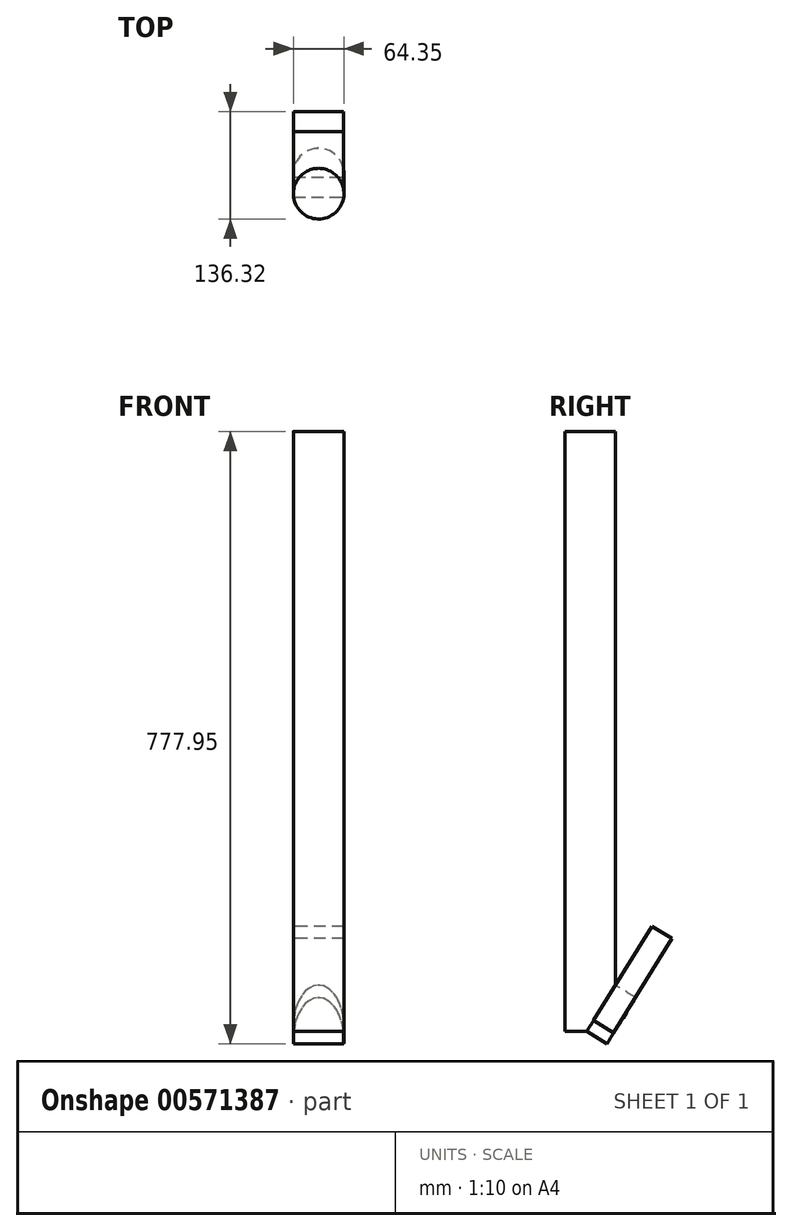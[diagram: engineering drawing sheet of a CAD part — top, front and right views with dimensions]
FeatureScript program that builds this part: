
annotation { "Feature Type Name" : "Feature", "Feature Type Description" : "" }
export const myFeature = defineFeature(function(context is Context, id is Id, definition is map)
    precondition{}
    {
        {
            var Q0;
            Q0=qCreatedBy(makeId("Top.planeOp"),FACE);
            var sketch = newSketch(context, id + "F0", { "sketchPlane" : qUnion([Q0])});
            skCircle(sketch, "E0", {"center": v(-58.01, -56.88) * mm, "radius": 32.18 * mm});
            skSolve(sketch);
        }
        {
            var Q0;
            Q0=makeQuery(id+"F0.imprint","IMPRINT",FACE,{"disambiguationData":[TD([[makeQuery(id+"F0.imprint","IMPRINT",EDGE,{"derivedFrom":sQuery(id+"F0.wireOp",EDGE,"E0")}),1.0]])]});
            extrude(context, id + "F1", {"entities" : qUnion([Q0]), "depth" : 762 * mm, "offsetDistance" : 25.4 * mm});
        }
        {
            var Q0;
            Q0=qCreatedBy(makeId("Right.planeOp"),FACE);
            var sketch = newSketch(context, id + "F2", { "sketchPlane" : qUnion([Q0])});
            skLineSegment(sketch, "E1", {"start": v(-61.23, 0) * mm, "end": v(13.2, 0) * mm});
            skLineSegment(sketch, "E2", {"start": v(13.2, 0) * mm, "end": v(13.2, 119.8) * mm});
            skLineSegment(sketch, "E3", {"start": v(13.2, 119.8) * mm, "end": v(-61.23, 0) * mm});
            skSolve(sketch);
        }
        {
            var Q0;
            Q0=makeQuery(id+"F2.imprint","IMPRINT",FACE,{"disambiguationData":[TD([[makeQuery(id+"F2.imprint","IMPRINT",EDGE,{"derivedFrom":sQuery(id+"F2.wireOp",EDGE,"E1")}),1.0]])]});
            var Q1;
            Q1=sQuery(id+"F2.wireOp",EDGE,"E2");
            var Q2;
            Q2=sQuery(id+"F2.wireOp",EDGE,"E3");
            var Q3;
            Q3=sQuery(id+"F2.wireOp",EDGE,"E1");
            extrude(context, id + "F3", {"entities" : qUnion([Q0]), "operationType" : NewBodyOperationType.REMOVE, "surfaceEntities" : qUnion([Q1, Q2, Q3]), "oppositeDirection" : true, "depth" : 146.56 * mm, "offsetDistance" : 25.4 * mm});
        }
        {
            var Q0;
            Q0=makeQuery(id+"F3.boolean.opBoolean","COPY",FACE,{"derivedFrom":makeQuery(id+"F3.opExtrude","SWEPT_FACE",FACE,{"disambiguationData":[OSD([sQuery(id+"F2.wireOp",EDGE,"E3")])]})});
            var sketch = newSketch(context, id + "F4", { "sketchPlane" : qUnion([Q0])});
            skLineSegment(sketch, "E4.bottom", {"start": v(26.13, -32.32) * mm, "end": v(89.9, -32.32) * mm});
            skLineSegment(sketch, "E4.top", {"start": v(26.13, 125.03) * mm, "end": v(89.9, 125.03) * mm});
            skLineSegment(sketch, "E4.left", {"start": v(26.13, -32.32) * mm, "end": v(26.13, 125.03) * mm});
            skLineSegment(sketch, "E4.right", {"start": v(89.9, -32.32) * mm, "end": v(89.9, 125.03) * mm});
            skSolve(sketch);
        }
        {
            var Q0;
            {var subQ0=sQuery(id+"F4.wireOp",EDGE,"E4.top");Q0=makeQuery(id+"F4.imprint","IMPRINT",FACE,{"disambiguationData":[TD([[makeQuery(id+"F4.imprint","IMPRINT",EDGE,{"derivedFrom":subQ0}),-1.0]])]});}
            extrude(context, id + "F5", {"entities" : qUnion([Q0]), "depth" : 29.97 * mm, "offsetDistance" : 25.4 * mm});
        }
        {
            var Q0;
            Q0=makeQuery(id+"F3.boolean.opBoolean","COPY",FACE,{"derivedFrom":makeQuery(id+"F3.opExtrude","SWEPT_FACE",FACE,{"disambiguationData":[OSD([sQuery(id+"F2.wireOp",EDGE,"E3")])]})});
            extrude(context, id + "F6", {"entities" : qUnion([Q0]), "depth" : 30.23 * mm, "offsetDistance" : 25.4 * mm});
        }
    });
